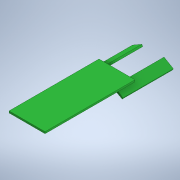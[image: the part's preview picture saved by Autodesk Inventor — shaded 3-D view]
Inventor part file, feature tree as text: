
AUTODESK INVENTOR PART (.ipt)
format: ipt  version: 2020 (Build 240168000, 168)  size: 115,712 bytes
history: native  units: mm
features: extrude x2, sketch x2
ambient origin geometry x8: Origin, YZ Plane, XZ Plane, XY Plane, X Axis, Y Axis, Z Axis, Center Point
bodies: Solid1 (feature_tree)
feature tree (4):
  extrude  "Extrusion1"  Depth=1.0mm
  extrude  "Extrusion2"  Depth=1.0mm
  sketch  "Sketch1"  dims[d0=20.0mm d1=1.0mm]
  sketch  "Sketch2"  dims[d2=50.0mm d3=0.0mm d4=1.0mm d6=12.365mm d7=120.0deg d8=6.0mm d9=20.0mm d10=8.0mm d11=0.0mm d12=0.0mm]
